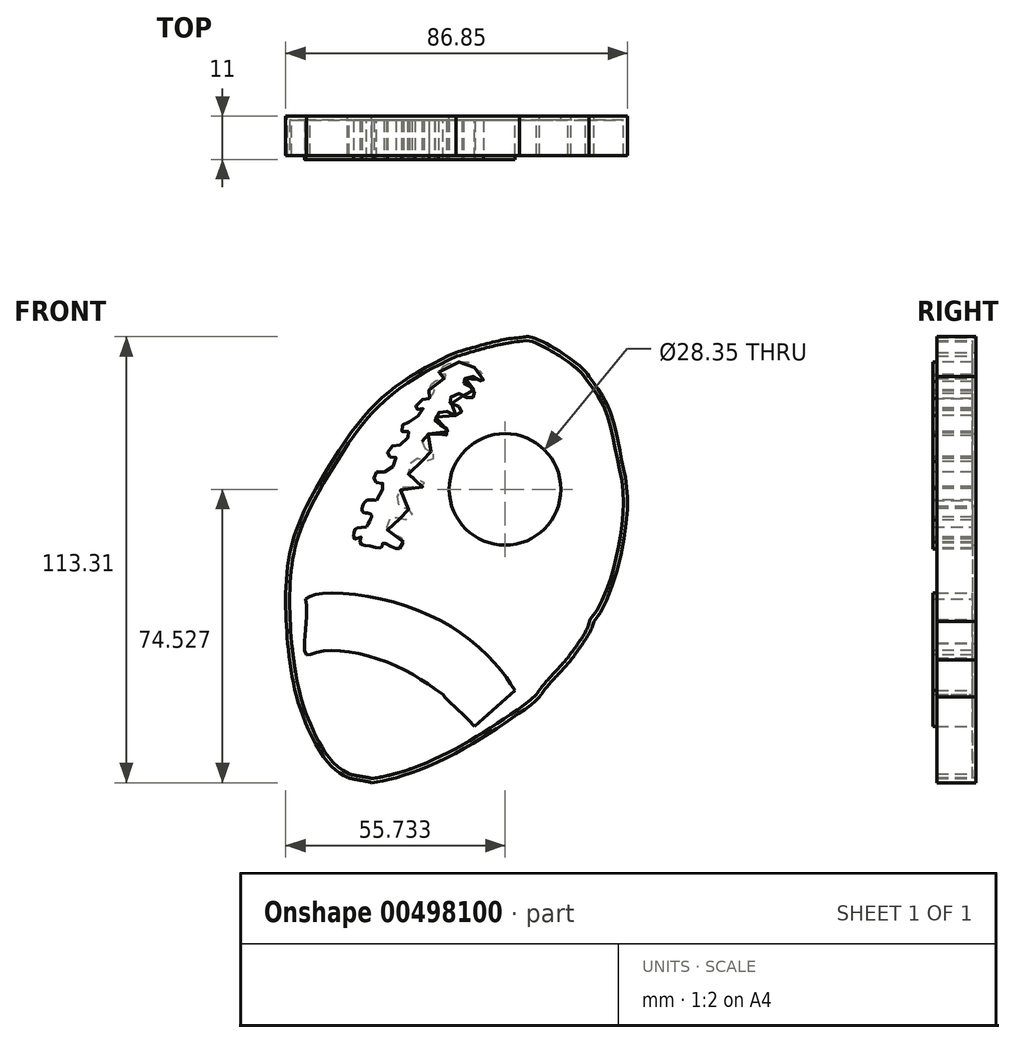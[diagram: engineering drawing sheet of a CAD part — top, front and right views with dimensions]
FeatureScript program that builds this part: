
annotation { "Feature Type Name" : "Feature", "Feature Type Description" : "" }
export const myFeature = defineFeature(function(context is Context, id is Id, definition is map)
    precondition{}
    {
        {
            var Q0;
            Q0=qCreatedBy(makeId("Front.planeOp"),FACE);
            var sketch = newSketch(context, id + "F0", { "sketchPlane" : qUnion([Q0])});
            skFitSpline(sketch, "E0", {"points": [v(-47.04, 4.8) * mm, v(-34.58, 24.87) * mm, v(-22.58, 36.4) * mm, v(-9.08, 43.85) * mm], "startDerivative": vector(26.52, 48.13) * mm, "endDerivative": vector(40.67, 19) * mm});
            skFitSpline(sketch, "E1", {"points": [v(-9.08, 43.85) * mm, v(7.07, 47.58) * mm], "startDerivative": vector(15.72, 4.27) * mm, "endDerivative": vector(13.99, 0.8) * mm});
            skFitSpline(sketch, "E2", {"points": [v(7.07, 47.58) * mm, v(10.47, 47.58) * mm, v(24.74, 37.75) * mm], "startDerivative": vector(13.67, 0.95) * mm, "endDerivative": vector(6.36, -13.27) * mm});
            skFitSpline(sketch, "E3", {"points": [v(24.74, 37.75) * mm, v(29.8, 29.63) * mm, v(32.93, 17.14) * mm, v(34.5, 3.49) * mm, v(25.98, -24.53) * mm], "startDerivative": vector(25.43, -34.1) * mm, "endDerivative": vector(-40.72, -44.45) * mm});
            skFitSpline(sketch, "E4", {"points": [v(-47.04, 4.8) * mm, v(-49.74, -1.76) * mm, v(-51.77, -10.4) * mm, v(-52.27, -21.27) * mm, v(-51.77, -30.12) * mm], "startDerivative": vector(-12.8, -28.42) * mm, "endDerivative": vector(2.58, -34.2) * mm});
            skFitSpline(sketch, "E5", {"points": [v(25.98, -24.53) * mm, v(20.18, -34.37) * mm], "startDerivative": vector(-1.76, -8.88) * mm, "endDerivative": vector(-6.7, -9.48) * mm});
            skFitSpline(sketch, "E6", {"points": [v(-51.77, -30.12) * mm, v(-50.36, -39.95) * mm, v(-47.15, -50.52) * mm, v(-41.02, -61) * mm, v(-36.63, -64.19) * mm], "startDerivative": vector(4.46, -38.43) * mm, "endDerivative": vector(23.03, -12.55) * mm});
            skFitSpline(sketch, "E7", {"points": [v(20.18, -34.37) * mm, v(12.25, -43.7) * mm], "startDerivative": vector(-7.42, -8.83) * mm, "endDerivative": vector(-5.17, -8.72) * mm});
            skFitSpline(sketch, "E8", {"points": [v(-36.63, -64.19) * mm, v(-30.46, -65.5) * mm], "startDerivative": vector(5.47, -1.67) * mm, "endDerivative": vector(5.47, -1.67) * mm});
            skFitSpline(sketch, "E9", {"points": [v(-30.46, -65.5) * mm, v(-23.4, -63.97) * mm, v(-8.76, -57.85) * mm, v(5.01, -49.22) * mm, v(12.25, -43.7) * mm, v(13.97, -40.78) * mm], "startDerivative": vector(37.23, 6.12) * mm, "endDerivative": vector(10.58, 24.1) * mm});
            skSolve(sketch);
        }
        {
            var Q0;
            Q0=makeQuery(id+"F0.imprint","IMPRINT",FACE,{"disambiguationData":[TD([[makeQuery(id+"F0.imprint","IMPRINT",EDGE,{"derivedFrom":sQuery(id+"F0.wireOp",EDGE,"E0")}),-1.0]])]});
            extrude(context, id + "F1", {"entities" : qUnion([Q0]), "depth" : 10 * mm, "offsetDistance" : 25 * mm});
        }
        {
            var Q0;
            Q0=makeQuery(id+"F1.opExtrude","CAP_FACE",FACE,{"disambiguationData":[OSD([sQuery(id+"F0.wireOp",EDGE,"E0"),sQuery(id+"F0.wireOp",EDGE,"E1"),sQuery(id+"F0.wireOp",EDGE,"E2"),sQuery(id+"F0.wireOp",EDGE,"E3"),sQuery(id+"F0.wireOp",EDGE,"E4"),sQuery(id+"F0.wireOp",EDGE,"E5"),sQuery(id+"F0.wireOp",EDGE,"E6"),sQuery(id+"F0.wireOp",EDGE,"E7"),sQuery(id+"F0.wireOp",EDGE,"E8"),sQuery(id+"F0.wireOp",EDGE,"E9")])],"isStart":false});
            shell(context, id + "F2", {"entities" : qUnion([Q0]), "thickness" : 1 * mm});
        }
        {
            var Q0;
            Q0=makeQuery(id+"F2.opShell","OFFSET_FACE",FACE,{"disambiguationData":[OSD([sQuery(id+"F0.wireOp",EDGE,"E0"),sQuery(id+"F0.wireOp",EDGE,"E1"),sQuery(id+"F0.wireOp",EDGE,"E2"),sQuery(id+"F0.wireOp",EDGE,"E3"),sQuery(id+"F0.wireOp",EDGE,"E4"),sQuery(id+"F0.wireOp",EDGE,"E5"),sQuery(id+"F0.wireOp",EDGE,"E6"),sQuery(id+"F0.wireOp",EDGE,"E7"),sQuery(id+"F0.wireOp",EDGE,"E8"),sQuery(id+"F0.wireOp",EDGE,"E9")])]});
            var sketch = newSketch(context, id + "F3", { "sketchPlane" : qUnion([Q0])});
            skFitSpline(sketch, "E10", {"points": [v(5.93, -42.06) * mm, v(-4.34, -51.24) * mm], "startDerivative": vector(-10.27, -9.18) * mm, "endDerivative": vector(-10.27, -9.18) * mm});
            skFitSpline(sketch, "E11", {"points": [v(5.93, -42.06) * mm, v(2.17, -36.63) * mm, v(-6.35, -28.55) * mm, v(-18.76, -21.69) * mm, v(-34.69, -17.65) * mm, v(-44.6, -17.68) * mm, v(-47.28, -18.78) * mm, v(-51.29, -19.58) * mm], "startDerivative": vector(-26.2, 42) * mm, "endDerivative": vector(-44.84, -6.26) * mm});
            skFitSpline(sketch, "E12", {"points": [v(-4.34, -51.24) * mm, v(-12.36, -43.1) * mm], "startDerivative": vector(-6.28, 8.14) * mm, "endDerivative": vector(-6.28, 8.14) * mm});
            skFitSpline(sketch, "E13", {"points": [v(-12.36, -43.1) * mm, v(-22.18, -36.8) * mm, v(-34.8, -32.5) * mm, v(-44.6, -32.39) * mm, v(-47.28, -32.67) * mm, v(-47.28, -18.78) * mm, v(-49.83, -19.37) * mm], "startDerivative": vector(-46.86, 33.68) * mm, "endDerivative": vector(-33.23, -22.64) * mm});
            skSolve(sketch);
        }
        {
            var Q0;
            {var subQ0=sQuery(id+"F3.wireOp",EDGE,"E10");Q0=makeQuery(id+"F3.imprint","IMPRINT",FACE,{"disambiguationData":[TD([[makeQuery(id+"F3.imprint","IMPRINT",EDGE,{"derivedFrom":subQ0}),-1.0]])]});}
            extrude(context, id + "F4", {"entities" : qUnion([Q0]), "operationType" : NewBodyOperationType.ADD, "depth" : 10 * mm, "offsetDistance" : 25 * mm});
        }
        {
            var Q0;
            Q0=makeQuery(id+"F2.opShell","OFFSET_FACE",FACE,{"disambiguationData":[OSD([sQuery(id+"F0.wireOp",EDGE,"E0"),sQuery(id+"F0.wireOp",EDGE,"E1"),sQuery(id+"F0.wireOp",EDGE,"E2"),sQuery(id+"F0.wireOp",EDGE,"E3"),sQuery(id+"F0.wireOp",EDGE,"E4"),sQuery(id+"F0.wireOp",EDGE,"E5"),sQuery(id+"F0.wireOp",EDGE,"E6"),sQuery(id+"F0.wireOp",EDGE,"E7"),sQuery(id+"F0.wireOp",EDGE,"E8"),sQuery(id+"F0.wireOp",EDGE,"E9")])]});
            var sketch = newSketch(context, id + "F5", { "sketchPlane" : qUnion([Q0])});
            skFitSpline(sketch, "E14", {"points": [v(15.68, 37.14) * mm, v(11.54, 39.32) * mm, v(5.23, 41.78) * mm, v(1.72, 43.23) * mm, v(-1.8, 43.6) * mm, v(-4.8, 44.01) * mm], "startDerivative": vector(-17.97, 10.54) * mm, "endDerivative": vector(-17.2, 2.85) * mm});
            skFitSpline(sketch, "E15", {"points": [v(15.68, 37.14) * mm, v(20.8, 33.71) * mm, v(23.18, 31.6) * mm], "startDerivative": vector(9.72, -6.12) * mm, "endDerivative": vector(5.02, -4.9) * mm});
            skFitSpline(sketch, "E16", {"points": [v(23.18, 31.6) * mm, v(27.57, 27.42) * mm, v(30.4, 24.4) * mm, v(27.28, 32.37) * mm, v(23.88, 37.23) * mm, v(18.67, 40.51) * mm, v(7.45, 45.78) * mm, v(4.02, 46.2) * mm, v(-4.8, 44.01) * mm], "startDerivative": vector(36.14, -30.5) * mm, "endDerivative": vector(-69.89, -19.72) * mm});
            skSolve(sketch);
        }
        {
            var Q0;
            {var subQ0=sQuery(id+"F0.wireOp",EDGE,"E3");var subQ1=sQuery(id+"F0.wireOp",EDGE,"E9");var subQ2=sQuery(id+"F0.wireOp",EDGE,"E8");var subQ3=sQuery(id+"F0.wireOp",EDGE,"E7");var subQ4=sQuery(id+"F0.wireOp",EDGE,"E6");var subQ5=sQuery(id+"F0.wireOp",EDGE,"E5");var subQ6=sQuery(id+"F0.wireOp",EDGE,"E0");var subQ7=sQuery(id+"F0.wireOp",EDGE,"E4");var subQ8=sQuery(id+"F0.wireOp",EDGE,"E1");var subQ9=sQuery(id+"F5.wireOp",EDGE,"E15");var subQ10=sQuery(id+"F5.wireOp",EDGE,"E16");var subQ11=makeQuery(id+"F2.opShell","OFFSET_EDGE",EDGE,{"disambiguationData":[OSD([subQ8]),TDD([makeQuery(id+"F1.opExtrude","CAP_EDGE",EDGE,{"disambiguationData":[OSD([subQ8])],"isStart":true})])]});var subQ12=makeQuery(id+"F5.imprint","INTERSECT",VERTEX,{"disambiguationData":[OD(2.0)],"derivedFrom":[subQ11,subQ10]});var subQ13=makeQuery(id+"F5.imprint","INTERSECT",VERTEX,{"disambiguationData":[OD(1.0)],"derivedFrom":[subQ11,subQ10]});var subQ14=makeQuery(id+"F2.opShell","OFFSET_EDGE",EDGE,{"disambiguationData":[OSD([subQ0]),TDD([makeQuery(id+"F1.opExtrude","CAP_EDGE",EDGE,{"disambiguationData":[OSD([subQ0])],"isStart":true})])]});var subQ15=sQuery(id+"F0.wireOp",EDGE,"E2");var subQ17=makeQuery(id+"F5.imprint","INTERSECT",VERTEX,{"disambiguationData":[OD(2.0)],"derivedFrom":[subQ14,subQ10]});var subQ18=makeQuery(id+"F5.imprint","INTERSECT",VERTEX,{"disambiguationData":[OD(1.0)],"derivedFrom":[subQ14,subQ10]});var subQ19=makeQuery(id+"F5.imprint","INTERSECT",VERTEX,{"disambiguationData":[OD(0.0)],"derivedFrom":[subQ14,subQ10]});Q0=makeQuery(id+"FMnKkGqeXD3epms_1.boolean.opBoolean","SPLIT",FACE,{"disambiguationData":[TD([makeQuery(id+"F2.opShell","OFFSET_FACE",FACE,{"disambiguationData":[OSD([subQ6])]}),makeQuery(id+"F2.opShell","OFFSET_FACE",FACE,{"disambiguationData":[OSD([subQ8])]}),makeQuery(id+"F2.opShell","OFFSET_FACE",FACE,{"disambiguationData":[OSD([subQ0])]}),makeQuery(id+"F2.opShell","OFFSET_FACE",FACE,{"disambiguationData":[OSD([subQ7])]}),makeQuery(id+"F2.opShell","OFFSET_FACE",FACE,{"disambiguationData":[OSD([subQ5])]}),makeQuery(id+"F2.opShell","OFFSET_FACE",FACE,{"disambiguationData":[OSD([subQ4])]}),makeQuery(id+"F2.opShell","OFFSET_FACE",FACE,{"disambiguationData":[OSD([subQ3])]}),makeQuery(id+"F2.opShell","OFFSET_FACE",FACE,{"disambiguationData":[OSD([subQ2])]}),makeQuery(id+"F2.opShell","OFFSET_FACE",FACE,{"disambiguationData":[OSD([subQ1])]}),makeQuery(id+"F4.opExtrude","SWEPT_FACE",FACE,{"disambiguationData":[OSD([sQuery(id+"F3.wireOp",EDGE,"E10")])]}),makeQuery(id+"F4.opExtrude","SWEPT_FACE",FACE,{"disambiguationData":[OSD([sQuery(id+"F3.wireOp",EDGE,"E11")])]}),makeQuery(id+"F4.opExtrude","SWEPT_FACE",FACE,{"disambiguationData":[OSD([sQuery(id+"F3.wireOp",EDGE,"E12")])]}),makeQuery(id+"F4.opExtrude","SWEPT_FACE",FACE,{"disambiguationData":[OSD([sQuery(id+"F3.wireOp",EDGE,"E13")])]}),makeQuery(id+"FMnKkGqeXD3epms_1.opExtrude","SWEPT_FACE",FACE,{"disambiguationData":[OSD([sQuery(id+"F5.wireOp",EDGE,"E14")])]}),makeQuery(id+"FMnKkGqeXD3epms_1.opExtrude","SWEPT_FACE",FACE,{"disambiguationData":[OSD([subQ9])]}),makeQuery(id+"FMnKkGqeXD3epms_1.opExtrude","SWEPT_FACE",FACE,{"disambiguationData":[OSD([subQ10]),TDD([makeQuery(id+"F5.imprint","IMPRINT",EDGE,{"disambiguationData":[TD([[makeQuery(id+"F5.imprint","INTERSECT",VERTEX,{"derivedFrom":[subQ9,subQ10]}),-1.0]])],"derivedFrom":subQ10}),makeQuery(id+"F5.imprint","IMPRINT",EDGE,{"disambiguationData":[TD([[subQ19,-1.0]])],"derivedFrom":subQ10}),makeQuery(id+"F5.imprint","IMPRINT",EDGE,{"disambiguationData":[TD([[subQ18,-1.0]])],"derivedFrom":subQ10}),makeQuery(id+"F5.imprint","IMPRINT",EDGE,{"disambiguationData":[TD([[subQ17,-1.0]])],"derivedFrom":subQ10}),makeQuery(id+"F5.imprint","IMPRINT",EDGE,{"disambiguationData":[TD([[subQ13,1.0]])],"derivedFrom":subQ10}),makeQuery(id+"F5.imprint","IMPRINT",EDGE,{"disambiguationData":[TD([[subQ13,-1.0]])],"derivedFrom":subQ10}),makeQuery(id+"F5.imprint","IMPRINT",EDGE,{"disambiguationData":[TD([[subQ12,-1.0]])],"derivedFrom":subQ10})])]})])],"derivedFrom":makeQuery(id+"F2.opShell","OFFSET_FACE",FACE,{"disambiguationData":[OSD([subQ6,subQ8,subQ15,subQ0,subQ7,subQ5,subQ4,subQ3,subQ2,subQ1])]})});}
            var sketch = newSketch(context, id + "F6", { "sketchPlane" : qUnion([Q0])});
            skFitSpline(sketch, "E17", {"points": [v(-22.35, -4.32) * mm, v(-23.03, -5.42) * mm, v(-24.03, -6.1) * mm, v(-27.52, -4.59) * mm, v(-27.87, -5.68) * mm, v(-30.75, -5.4) * mm, v(-33.27, -4.75) * mm, v(-33.2, -3.41) * mm, v(-33.04, -3.08) * mm, v(-34.65, -3.58) * mm, v(-34.93, -1.96) * mm, v(-34.5, -0.98) * mm, v(-31.76, -0.48) * mm], "startDerivative": vector(-9.33, -14.76) * mm, "endDerivative": vector(31.6, 2.44) * mm});
            skFitSpline(sketch, "E18", {"points": [v(-31.76, -0.48) * mm, v(-30.6, 2.7) * mm, v(-32.48, 3.17) * mm, v(-32.82, 4.54) * mm, v(-31.76, 6.15) * mm, v(-29.21, 6.2) * mm], "startDerivative": vector(9.68, 16.42) * mm, "endDerivative": vector(13.2, -1.97) * mm});
            skFitSpline(sketch, "E19", {"points": [v(-29.21, 6.2) * mm, v(-27.48, 10.42) * mm, v(-29.21, 10.77) * mm, v(-29.89, 11.64) * mm, v(-29.21, 13.37) * mm, v(-26, 13.79) * mm, v(-24.38, 17.35) * mm, v(-26.25, 17.23) * mm, v(-25.63, 19.84) * mm, v(-22.85, 20.48) * mm, v(-20.9, 23.6) * mm, v(-22.58, 23.6) * mm, v(-22.57, 25.42) * mm, v(-19.97, 26.6) * mm, v(-17.41, 29.66) * mm, v(-19.32, 29.32) * mm, v(-18.14, 31.55) * mm, v(-15.78, 32.1) * mm], "startDerivative": vector(42, 69.73) * mm, "endDerivative": vector(41.2, -2.39) * mm});
            skFitSpline(sketch, "E20", {"points": [v(-15.78, 32.1) * mm, v(-14.45, 34.23) * mm, v(-15.78, 34.06) * mm, v(-14.4, 36.55) * mm, v(-12.2, 37.04) * mm, v(-11.55, 38.2) * mm, v(-13.36, 38.13) * mm, v(-12.23, 40.17) * mm, v(-8.73, 41.37) * mm, v(-5.12, 41.07) * mm, v(-4.56, 40.17) * mm, v(-3.2, 39.2) * mm, v(-2.23, 37.91) * mm, v(-2.27, 36.48) * mm, v(-5.43, 37.84) * mm, v(-7.15, 36.14) * mm, v(-5.46, 35.2) * mm, v(-4.23, 33.14) * mm, v(-5.49, 32.1) * mm, v(-8.73, 33.35) * mm, v(-10.78, 31.34) * mm, v(-7.62, 29.57) * mm, v(-8.73, 27.8) * mm, v(-12.45, 29.07) * mm, v(-14.24, 26.18) * mm, v(-11.53, 24.66) * mm, v(-11.48, 22.8) * mm, v(-15.78, 23.2) * mm, v(-17.5, 19.95) * mm, v(-14.55, 17.98) * mm, v(-15.78, 16.06) * mm, v(-19.36, 16.75) * mm, v(-21.1, 12.9) * mm, v(-17.24, 10.92) * mm, v(-18.13, 9.32) * mm, v(-22.05, 9.7) * mm, v(-23.96, 5.38) * mm, v(-20.2, 3.35) * mm, v(-21.82, 1.32) * mm, v(-25.2, 1.92) * mm, v(-26.6, -0.98) * mm, v(-23.03, -3.2) * mm, v(-22.35, -4.32) * mm, v(-22.57, -4.68) * mm], "startDerivative": vector(109.14, 136.28) * mm, "endDerivative": vector(-32.43, -32.14) * mm});
            skSolve(sketch);
        }
        {
            var Q0;
            {var subQ1=sQuery(id+"F6.wireOp",EDGE,"E18");Q0=makeQuery(id+"F6.imprint","IMPRINT",FACE,{"disambiguationData":[TD([[makeQuery(id+"F6.imprint","IMPRINT",EDGE,{"derivedFrom":subQ1}),-1.0]])]});}
            extrude(context, id + "F7", {"entities" : qUnion([Q0]), "operationType" : NewBodyOperationType.ADD, "depth" : 10 * mm, "offsetDistance" : 25 * mm});
        }
        {
            var Q0;
            Q0=qCreatedBy(makeId("Front.planeOp"),FACE);
            var sketch = newSketch(context, id + "F8", { "sketchPlane" : qUnion([Q0])});
            skCircle(sketch, "E21", {"center": v(3.44, 9.04) * mm, "radius": 14.17 * mm});
            skSolve(sketch);
        }
        {
            var Q0;
            Q0 = qSketchRegion(id + "F8", true);
            extrude(context, id + "F9", {"entities" : qUnion([Q0]), "operationType" : NewBodyOperationType.REMOVE, "depth" : 25 * mm, "offsetDistance" : 25 * mm});
        }
    });
